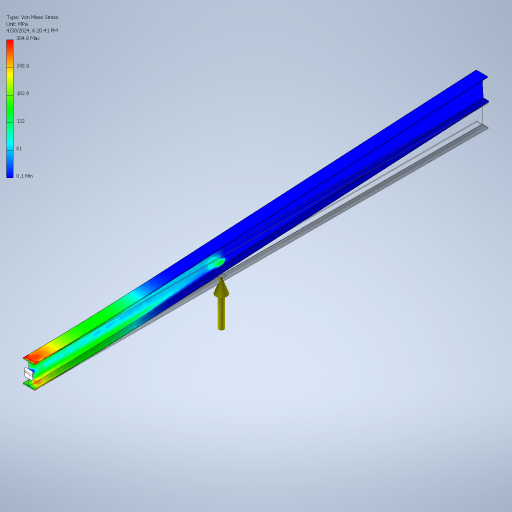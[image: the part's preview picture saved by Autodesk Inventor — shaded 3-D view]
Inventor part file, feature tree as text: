
AUTODESK INVENTOR PART (.ipt)
format: ipt  version: 2024 (Build 280153000, 153)  size: 334,336 bytes
history: native  units: mm
features: sketch x3, extrude x2
ambient origin geometry x8: Origin, YZ Plane, XZ Plane, XY Plane, X Axis, Y Axis, Z Axis, Center Point
bodies: Solid1 (feature_tree)
feature tree (5):
  sketch  "Sketch1"  dims[d0=100.0mm d1=2.0mm]
  extrude  "Extrusion1"  Depth=2.0mm
  extrude  "Extrusion2"  Depth=7.589mm
  sketch  "Sketch2"  dims[d2=7.589mm d3=7.589mm]
  sketch  "Sketch3"  dims[d4=200.0mm d5=4000.0mm d6=0.0mm d8=50.0mm d10=0.1mm d11=0.0mm d12=1697.6mm d7=0.5mm]
